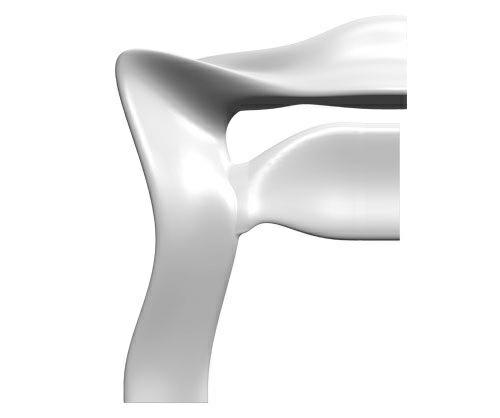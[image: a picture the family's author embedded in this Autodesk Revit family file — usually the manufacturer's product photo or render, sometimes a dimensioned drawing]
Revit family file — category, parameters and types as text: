
# Revit family: CITY ALPHABET letter „F”
name_source: partatom
category: Furniture
revit_build: Autodesk Revit 2018 (Build: 20190510_1515(x64)
units: mm (PartAtom-declared; Revit-internal decimal feet)

## family parameters
Cut with Voids When Loaded = No
Host = Face
OmniClass Number = 23.40.10.11.14
OmniClass Title = Exterior Seating
Room Calculation Point = No
Shared = No

## types (1)
- CITY ALPHABET letter „F”
    Default Elevation = 1219 mm
    Height = 1100 mm
    IfcExportAs = IfcFurnishingElement
    Length = 2190 mm  [stored 7.18504 ft]
    Manufacturer = Astrini Design
    Material information = Colour choice from RAL colour standard. Customer may inquire about specific request regarding individual order.
    Model = CITY ALPHABET letter „F”
    Operating temperature = -40°C to 80°C, ( -40°F to 176°F )
    Type Comments = Bench
    Type Image = F.jpg
    URL = https://astrini-design.pl
    Weight (approximately) = 62.00 kg
    Weight - filled (approximately) = 112.00 kg
    Width = 1650 mm  [stored 5.41339 ft]

note: [stored X ft] marks values corroborated as IEEE doubles in the binary element streams (Revit-internal decimal feet)
